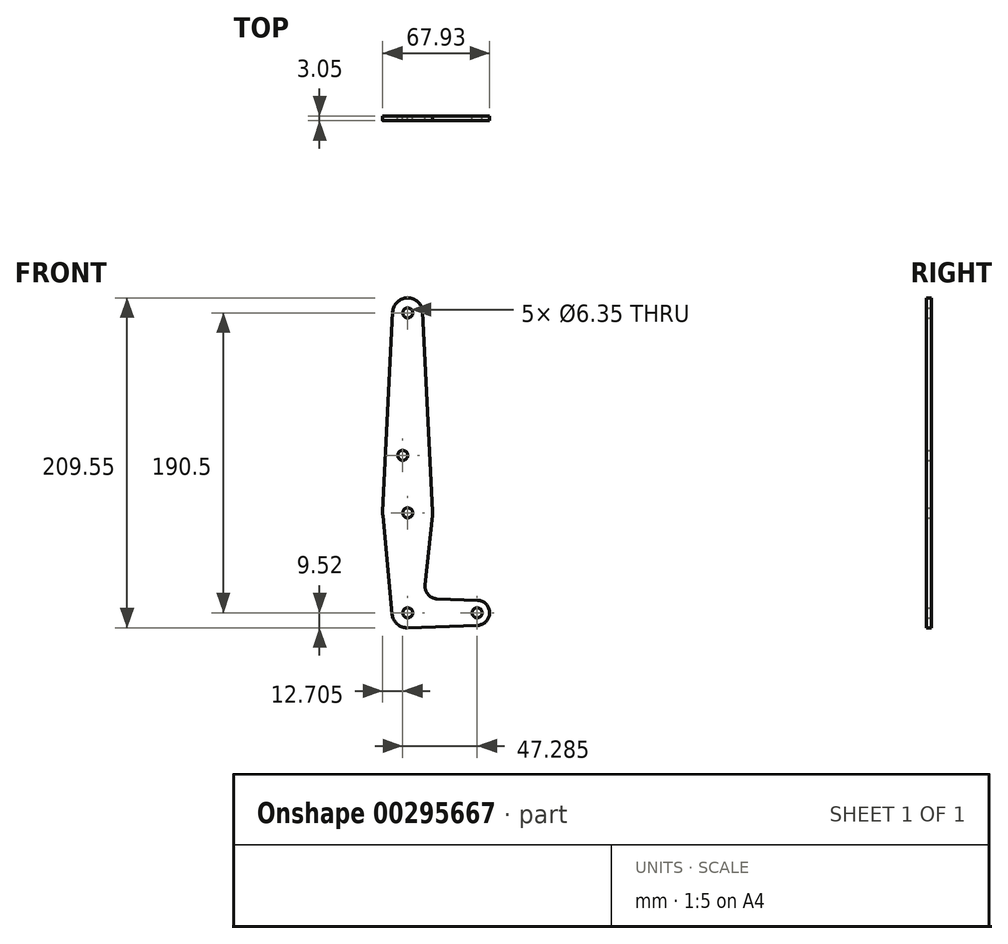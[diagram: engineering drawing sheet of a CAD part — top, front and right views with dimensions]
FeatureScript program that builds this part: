
annotation { "Feature Type Name" : "Feature", "Feature Type Description" : "" }
export const myFeature = defineFeature(function(context is Context, id is Id, definition is map)
    precondition{}
    {
        {
            var Q0;
            Q0=qCreatedBy(makeId("Front.planeOp"),FACE);
            var sketch = newSketch(context, id + "F0", { "sketchPlane" : qUnion([Q0])});
            skCircle(sketch, "E0", {"center": v(0, 190.5) * mm, "radius": 9.53 * mm});
            skCircle(sketch, "E1", {"center": v(0, 63.5) * mm, "radius": 15.88 * mm});
            skCircle(sketch, "E2", {"center": v(-0.34, 0) * mm, "radius": 9.53 * mm});
            skCircle(sketch, "E3", {"center": v(44.1, 0) * mm, "radius": 7.94 * mm});
            skLineSegment(sketch, "E4", {"start": v(0, 190.5) * mm, "end": v(0, 63.5) * mm, "construction": true});
            skLineSegment(sketch, "E5", {"start": v(0, 63.5) * mm, "end": v(-0.34, 0) * mm, "construction": true});
            skLineSegment(sketch, "E6", {"start": v(-0.34, 0) * mm, "end": v(44.1, 0) * mm, "construction": true});
            skLineSegment(sketch, "E7", {"start": v(-9.51, 190.98) * mm, "end": v(-15.86, 64.3) * mm});
            skLineSegment(sketch, "E8", {"start": v(-15.8, 62) * mm, "end": v(-9.82, -0.9) * mm});
            skLineSegment(sketch, "E9", {"start": v(9.51, 190.98) * mm, "end": v(15.86, 64.3) * mm});
            skLineSegment(sketch, "E10", {"start": v(15.79, 61.83) * mm, "end": v(11.1, 17.63) * mm});
            skLineSegment(sketch, "E11", {"start": v(18.73, 8.85) * mm, "end": v(44.4, 7.93) * mm});
            skLineSegment(sketch, "E12", {"start": v(0, -9.52) * mm, "end": v(44.4, -7.93) * mm});
            skCircle(sketch, "E13", {"center": v(0, 190.5) * mm, "radius": 3.18 * mm});
            skCircle(sketch, "E14", {"center": v(0, 63.5) * mm, "radius": 3.18 * mm});
            skCircle(sketch, "E15", {"center": v(0, 0) * mm, "radius": 3.18 * mm});
            skCircle(sketch, "E16", {"center": v(44.1, 0) * mm, "radius": 3.18 * mm});
            skCircle(sketch, "E17", {"center": v(-3.17, 100.03) * mm, "radius": 3.18 * mm});
            skPoint(sketch, "E18.newPointB", {"position": v(0, 9.52) * mm});
            skArc(sketch, "E18.filletArc", {"start": v(11.1, 17.63) * mm, "mid": v(13, 11.58) * mm, "end": v(18.73, 8.85) * mm});
            skSolve(sketch);
        }
        {
            var Q0;
            Q0 = qSketchRegion(id + "F0", true);
            extrude(context, id + "F1", {"entities" : qUnion([Q0]), "depth" : 3.05 * mm});
        }
    });
